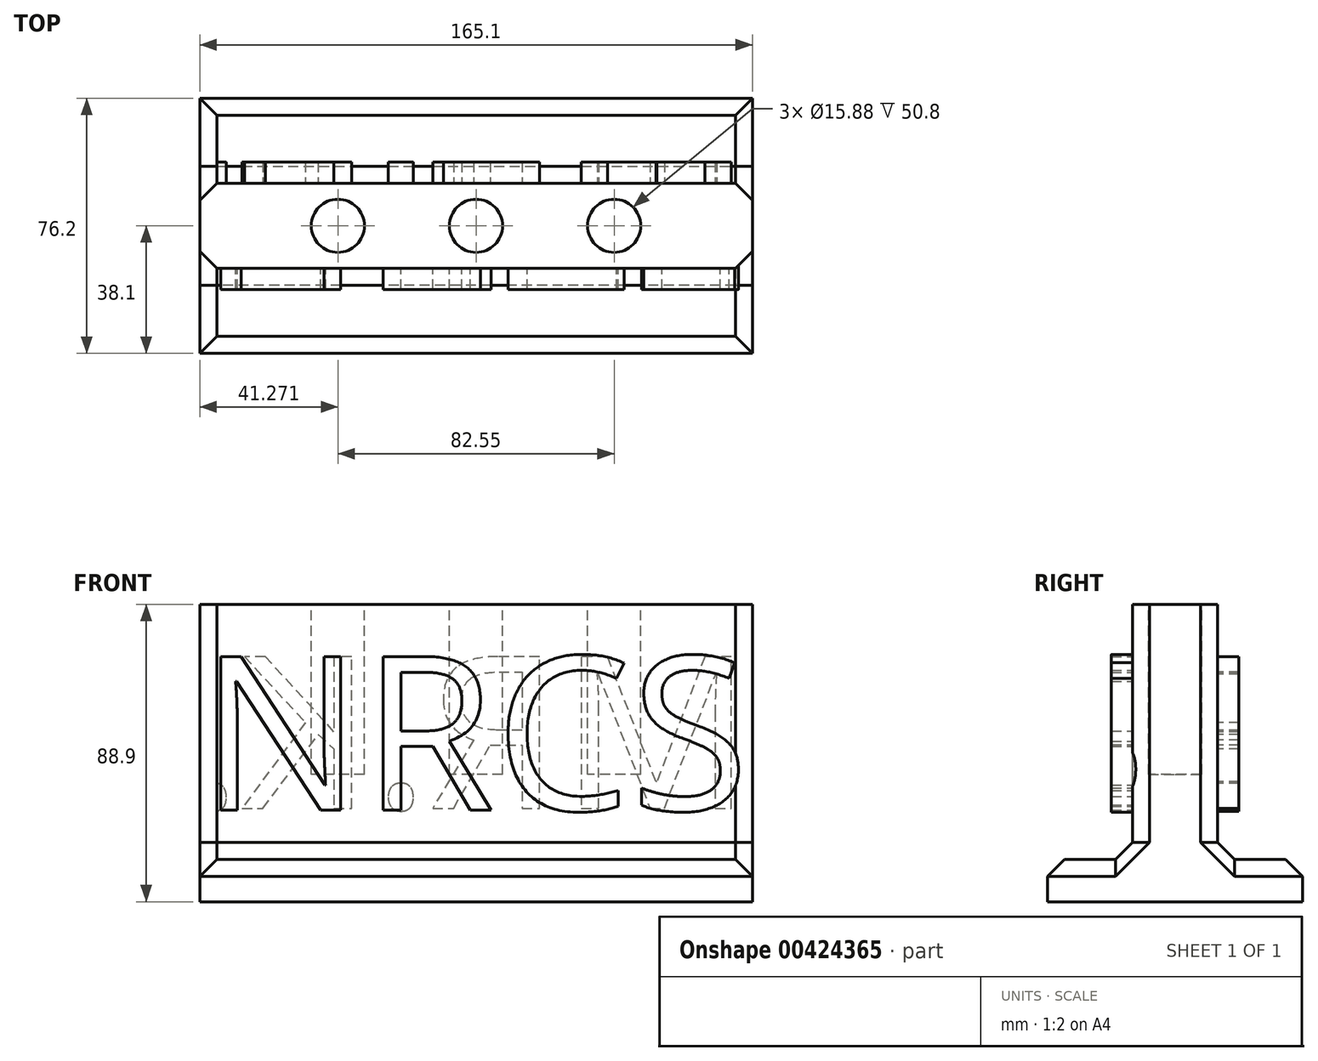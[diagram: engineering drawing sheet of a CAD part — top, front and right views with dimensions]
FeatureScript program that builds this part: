
annotation { "Feature Type Name" : "Feature", "Feature Type Description" : "" }
export const myFeature = defineFeature(function(context is Context, id is Id, definition is map)
    precondition{}
    {
        {
            var Q0;
            Q0=qCreatedBy(makeId("Front.planeOp"),FACE);
            var sketch = newSketch(context, id + "F0", { "sketchPlane" : qUnion([Q0])});
            skLineSegment(sketch, "E0.bottom", {"start": v(-68.78, -42.25) * mm, "end": v(96.32, -42.25) * mm});
            skLineSegment(sketch, "E0.top", {"start": v(-68.78, 33.95) * mm, "end": v(96.32, 33.95) * mm});
            skLineSegment(sketch, "E0.left", {"start": v(-68.78, -42.25) * mm, "end": v(-68.78, 33.95) * mm});
            skLineSegment(sketch, "E0.right", {"start": v(96.32, -42.25) * mm, "end": v(96.32, 33.95) * mm});
            skSolve(sketch);
        }
        {
            var Q0;
            Q0 = qSketchRegion(id + "F0", true);
            extrude(context, id + "F1", {"entities" : qUnion([Q0]), "depth" : 25.4 * mm});
        }
        {
            var Q0;
            Q0=makeQuery(id+"F1.opExtrude","CAP_FACE",FACE,{"disambiguationData":[OSD([sQuery(id+"F0.wireOp",EDGE,"E0.bottom"),sQuery(id+"F0.wireOp",EDGE,"E0.top"),sQuery(id+"F0.wireOp",EDGE,"E0.left"),sQuery(id+"F0.wireOp",EDGE,"E0.right")])],"isStart":false});
            var sketch = newSketch(context, id + "F2", { "sketchPlane" : qUnion([Q0])});
            skText(sketch, "E1", { "text": "NRCS", "fontName": "OpenSans-Regular.ttf"});
            const initialGuessF2  = {"E1": [-0.06878, -0.02757, 1, 0, 0.04628]};
            skSetInitialGuess(sketch, initialGuessF2);
            skSolve(sketch);
        }
        {
            var Q0;
            Q0 = qSketchRegion(id + "F2", true);
            extrude(context, id + "F3", {"entities" : qUnion([Q0]), "operationType" : NewBodyOperationType.ADD, "depth" : 6.35 * mm});
        }
        {
            var Q0;
            Q0=makeQuery(id+"F1.opExtrude","SWEPT_FACE",FACE,{"disambiguationData":[OSD([sQuery(id+"F0.wireOp",EDGE,"E0.top")])]});
            var sketch = newSketch(context, id + "F4", { "sketchPlane" : qUnion([Q0])});
            skCircle(sketch, "E2", {"center": v(13.77, -12.7) * mm, "radius": 7.94 * mm});
            skPoint(sketch, "E2.centerSnap0", {"position": v(96.32, -12.7) * mm});
            skPoint(sketch, "E2.centerSnap1", {"position": v(13.77, 0) * mm});
            skLineSegment(sketch, "E3", {"start": v(13.77, 0) * mm, "end": v(-68.78, 0) * mm});
            skCircle(sketch, "E4", {"center": v(-27.5, -12.7) * mm, "radius": 7.94 * mm});
            skPoint(sketch, "E4.centerSnap0", {"position": v(-27.5, 0) * mm});
            skLineSegment(sketch, "E5", {"start": v(13.77, 0) * mm, "end": v(96.32, 0) * mm});
            skCircle(sketch, "E6", {"center": v(55.04, -12.7) * mm, "radius": 7.94 * mm});
            skPoint(sketch, "E6.centerSnap0", {"position": v(55.04, 0) * mm});
            skSolve(sketch);
        }
        {
            var Q0;
            Q0=makeQuery(id+"F4.imprint","IMPRINT",FACE,{"disambiguationData":[TD([[makeQuery(id+"F4.imprint","IMPRINT",EDGE,{"derivedFrom":sQuery(id+"F4.wireOp",EDGE,"E4")}),1.0]])]});
            var Q1;
            Q1=makeQuery(id+"F4.imprint","IMPRINT",FACE,{"disambiguationData":[TD([[makeQuery(id+"F4.imprint","IMPRINT",EDGE,{"derivedFrom":sQuery(id+"F4.wireOp",EDGE,"E2")}),1.0]])]});
            var Q2;
            Q2=makeQuery(id+"F4.imprint","IMPRINT",FACE,{"disambiguationData":[TD([[makeQuery(id+"F4.imprint","IMPRINT",EDGE,{"derivedFrom":sQuery(id+"F4.wireOp",EDGE,"E6")}),1.0]])]});
            extrude(context, id + "F5", {"entities" : qUnion([Q0, Q1, Q2]), "operationType" : NewBodyOperationType.REMOVE, "oppositeDirection" : true, "depth" : 50.8 * mm});
        }
        {
            var Q0;
            Q0=makeQuery(id+"F1.opExtrude","SWEPT_FACE",FACE,{"disambiguationData":[OSD([sQuery(id+"F0.wireOp",EDGE,"E0.bottom")])]});
            var sketch = newSketch(context, id + "F6", { "sketchPlane" : qUnion([Q0])});
            skLineSegment(sketch, "E7.bottom", {"start": v(-68.78, 50.8) * mm, "end": v(96.32, 50.8) * mm});
            skLineSegment(sketch, "E7.top", {"start": v(-68.78, -25.4) * mm, "end": v(96.32, -25.4) * mm});
            skLineSegment(sketch, "E7.left", {"start": v(-68.78, 50.8) * mm, "end": v(-68.78, -25.4) * mm});
            skLineSegment(sketch, "E7.right", {"start": v(96.32, 50.8) * mm, "end": v(96.32, -25.4) * mm});
            skPoint(sketch, "E7.middle", {"position": v(13.77, 12.7) * mm});
            skPoint(sketch, "E7.middle.positionSnap0", {"position": v(13.77, 0) * mm});
            skPoint(sketch, "E7.middle.positionSnap1", {"position": v(-68.78, 12.7) * mm});
            skPoint(sketch, "E7.centerSnap0", {"position": v(13.77, 0) * mm});
            skPoint(sketch, "E7.centerSnap1", {"position": v(-68.78, 12.7) * mm});
            skSolve(sketch);
        }
        {
            var Q0;
            Q0 = qSketchRegion(id + "F6", true);
            extrude(context, id + "F7", {"entities" : qUnion([Q0]), "operationType" : NewBodyOperationType.ADD, "depth" : 12.7 * mm});
        }
        {
            var Q0;
            {var subQ1=sQuery(id+"F6.wireOp",EDGE,"E7.right");var subQ2=sQuery(id+"F6.wireOp",EDGE,"E7.top");var subQ4=sQuery(id+"F6.wireOp",EDGE,"E7.left");Q0=makeQuery(id+"F7.boolean.opBoolean","SPLIT",FACE,{"disambiguationData":[TD([makeQuery(id+"F7.opExtrude","SWEPT_FACE",FACE,{"disambiguationData":[OSD([subQ2])]})])],"derivedFrom":makeQuery(id+"F7.opExtrude","CAP_FACE",FACE,{"disambiguationData":[OSD([sQuery(id+"F6.wireOp",EDGE,"E7.bottom"),subQ2,subQ4,subQ1])],"isStart":true})});}
            chamfer(context, id + "F8", {"entities" : qUnion([Q0]), "width" : 5.08 * mm, "tangentPropagation" : true});
        }
        {
            var Q0;
            {var subQ0=sQuery(id+"F6.wireOp",EDGE,"E7.bottom");var subQ2=sQuery(id+"F6.wireOp",EDGE,"E7.right");var subQ4=sQuery(id+"F6.wireOp",EDGE,"E7.left");Q0=makeQuery(id+"F7.boolean.opBoolean","SPLIT",FACE,{"disambiguationData":[TD([makeQuery(id+"F7.opExtrude","SWEPT_FACE",FACE,{"disambiguationData":[OSD([subQ0])]})])],"derivedFrom":makeQuery(id+"F7.opExtrude","CAP_FACE",FACE,{"disambiguationData":[OSD([subQ0,sQuery(id+"F6.wireOp",EDGE,"E7.top"),subQ4,subQ2])],"isStart":true})});}
            chamfer(context, id + "F9", {"entities" : qUnion([Q0]), "width" : 5.08 * mm, "tangentPropagation" : true});
        }
        {
            var Q0;
            Q0=makeQuery(id+"F1.opExtrude","CAP_FACE",FACE,{"disambiguationData":[OSD([sQuery(id+"F0.wireOp",EDGE,"E0.bottom"),sQuery(id+"F0.wireOp",EDGE,"E0.top"),sQuery(id+"F0.wireOp",EDGE,"E0.left"),sQuery(id+"F0.wireOp",EDGE,"E0.right")])],"isStart":true});
            var sketch = newSketch(context, id + "F10", { "sketchPlane" : qUnion([Q0])});
            skLineSegment(sketch, "E8", {"start": v(-96.32, 33.95) * mm, "end": v(-96.32, 18.7) * mm});
            skLineSegment(sketch, "E9", {"start": v(72.44, -42.25) * mm, "end": v(72.44, -27.01) * mm});
            skText(sketch, "E10", { "text": "MR.K.", "fontName": "OpenSans-Regular.ttf"});
            const initialGuessF10  = {"E10": [-0.09632, -0.02701, 1, 0, 0.04572]};
            skSetInitialGuess(sketch, initialGuessF10);
            skSolve(sketch);
        }
        {
            var Q0;
            Q0=makeQuery(id+"F10.imprint","IMPRINT",FACE,{"disambiguationData":[TD([[makeQuery(id+"F10.imprint","IMPRINT",EDGE,{"derivedFrom":sQuery(id+"F10.wireOp",EDGE,"E10.sketch_text.stroke-0")}),-1.0]])]});
            var Q1;
            Q1=makeQuery(id+"F10.imprint","IMPRINT",FACE,{"disambiguationData":[TD([[makeQuery(id+"F10.imprint","IMPRINT",EDGE,{"derivedFrom":sQuery(id+"F10.wireOp",EDGE,"E10.sketch_text.stroke-18")}),-1.0]])]});
            var Q2;
            Q2=makeQuery(id+"F10.imprint","IMPRINT",FACE,{"disambiguationData":[TD([[makeQuery(id+"F10.imprint","IMPRINT",EDGE,{"derivedFrom":sQuery(id+"F10.wireOp",EDGE,"E10.sketch_text.stroke-44")}),-1.0]])]});
            var Q3;
            Q3=makeQuery(id+"F10.imprint","IMPRINT",FACE,{"disambiguationData":[TD([[makeQuery(id+"F10.imprint","IMPRINT",EDGE,{"derivedFrom":sQuery(id+"F10.wireOp",EDGE,"E10.sketch_text.stroke-36")}),-1.0]])]});
            var Q4;
            Q4=makeQuery(id+"F10.imprint","IMPRINT",FACE,{"disambiguationData":[TD([[makeQuery(id+"F10.imprint","IMPRINT",EDGE,{"derivedFrom":sQuery(id+"F10.wireOp",EDGE,"E10.sketch_text.stroke-56")}),-1.0]])]});
            extrude(context, id + "F11", {"entities" : qUnion([Q0, Q1, Q2, Q3, Q4]), "operationType" : NewBodyOperationType.ADD, "depth" : 6.35 * mm});
        }
    });
